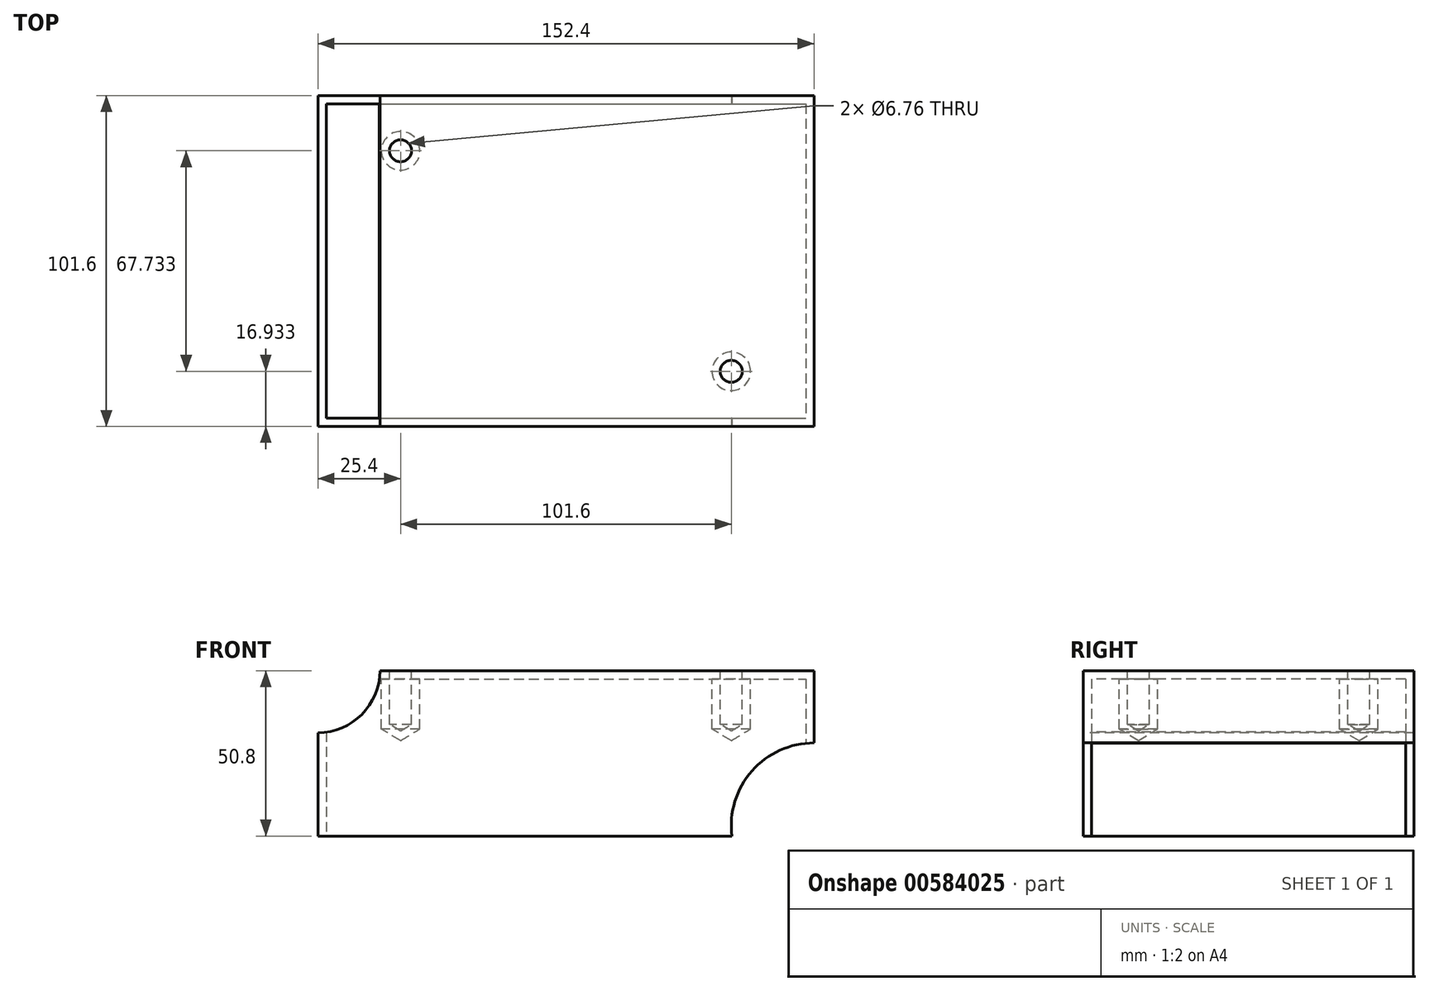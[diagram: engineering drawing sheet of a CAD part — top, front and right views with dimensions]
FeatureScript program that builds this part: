
annotation { "Feature Type Name" : "Feature", "Feature Type Description" : "" }
export const myFeature = defineFeature(function(context is Context, id is Id, definition is map)
    precondition{}
    {
        {
            var Q0;
            Q0=qCreatedBy(makeId("Top.planeOp"),FACE);
            var sketch = newSketch(context, id + "F0", { "sketchPlane" : qUnion([Q0])});
            skLineSegment(sketch, "E0.bottom", {"start": v(-76.2, 50.8) * mm, "end": v(76.2, 50.8) * mm});
            skLineSegment(sketch, "E0.top", {"start": v(-76.2, -50.8) * mm, "end": v(76.2, -50.8) * mm});
            skLineSegment(sketch, "E0.left", {"start": v(-76.2, 50.8) * mm, "end": v(-76.2, -50.8) * mm});
            skLineSegment(sketch, "E0.right", {"start": v(76.2, 50.8) * mm, "end": v(76.2, -50.8) * mm});
            skSolve(sketch);
        }
        {
            var Q0;
            Q0 = qSketchRegion(id + "F0", true);
            extrude(context, id + "F1", {"entities" : qUnion([Q0]), "depth" : 50.8 * mm, "offsetDistance" : 25.4 * mm});
        }
        {
            var Q0;
            Q0=makeQuery(id+"F1.opExtrude","CAP_FACE",FACE,{"disambiguationData":[OSD([sQuery(id+"F0.wireOp",EDGE,"E0.bottom"),sQuery(id+"F0.wireOp",EDGE,"E0.top"),sQuery(id+"F0.wireOp",EDGE,"E0.left"),sQuery(id+"F0.wireOp",EDGE,"E0.right")])],"isStart":false});
            var sketch = newSketch(context, id + "F2", { "sketchPlane" : qUnion([Q0])});
            skLineSegment(sketch, "E1", {"start": v(-76.2, 50.8) * mm, "end": v(76.2, -50.8) * mm});
            skPoint(sketch, "E2", {"position": v(-50.8, 33.87) * mm});
            skPoint(sketch, "E3", {"position": v(50.8, -33.87) * mm});
            skSolve(sketch);
        }
        {
            var Q0;
            Q0=sQuery(id+"F2.wireOp",VERTEX,"E2");
            var Q1;
            Q1=sQuery(id+"F2.wireOp",VERTEX,"E3");
            var Q2;
            Q2=makeQuery(id+"F1.opExtrude","SWEPT_BODY",BODY,{"disambiguationData":[OSD([sQuery(id+"F0.wireOp",EDGE,"E0.bottom"),sQuery(id+"F0.wireOp",EDGE,"E0.top"),sQuery(id+"F0.wireOp",EDGE,"E0.left"),sQuery(id+"F0.wireOp",EDGE,"E0.right")])]});
            hole(context, id + "F3", {"style" : HoleStyle.SIMPLE, "endStyle" : HoleEndStyle.BLIND, "standardTappedOrClearance" : lookupTablePath({ "standard" : "ANSI", "fit" : "Normal (ASME)", "size" : "1/4", "type" : "Clearance" }), "standardBlindInLast" : lookupTablePath({ "fit" : "Free", "standard" : "ANSI", "size" : "1/4", "type" : "Clearance" }), "holeDiameter" : 6.76 * mm, "majorDiameter" : 6.35 * mm, "holeDepth" : 16.51 * mm, "isTappedThrough" : true, "tappedDepth" : 12.7 * mm, "tapClearance" : 3, "locations" : qUnion([Q0, Q1]), "scope" : qUnion([Q2])});
        }
        {
            var Q0;
            Q0=makeQuery(id+"F1.opExtrude","CAP_FACE",FACE,{"disambiguationData":[OSD([sQuery(id+"F0.wireOp",EDGE,"E0.bottom"),sQuery(id+"F0.wireOp",EDGE,"E0.top"),sQuery(id+"F0.wireOp",EDGE,"E0.left"),sQuery(id+"F0.wireOp",EDGE,"E0.right")])],"isStart":true});
            shell(context, id + "F4", {"entities" : qUnion([Q0]), "thickness" : 2.54 * mm});
        }
        {
            var Q0;
            Q0=makeQuery(id+"F1.opExtrude","SWEPT_FACE",FACE,{"disambiguationData":[OSD([sQuery(id+"F0.wireOp",EDGE,"E0.top")])]});
            var sketch = newSketch(context, id + "F5", { "sketchPlane" : qUnion([Q0])});
            skCircle(sketch, "E4", {"center": v(-76.2, 50.8) * mm, "radius": 19.05 * mm});
            skCircle(sketch, "E5", {"center": v(76.2, 3.2) * mm, "radius": 25.4 * mm});
            skSolve(sketch);
        }
        {
            var Q0;
            Q0 = qSketchRegion(id + "F5", true);
            extrude(context, id + "F6", {"entities" : qUnion([Q0]), "operationType" : NewBodyOperationType.REMOVE, "oppositeDirection" : true, "depth" : 135.89 * mm, "offsetDistance" : 25.4 * mm});
        }
    });
